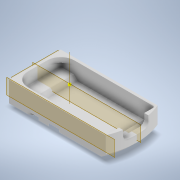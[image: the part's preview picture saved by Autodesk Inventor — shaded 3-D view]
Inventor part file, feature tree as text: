
AUTODESK INVENTOR PART (.ipt)
format: ipt  version: 2021 (Build 250183000, 183)  size: 813,056 bytes
history: native  units: in
note: dims shown in document units (in); Inventor stores cm internally (conversion verified against a paired STEP export)
features: sketch x10, extrude x9, fillet x4, chamfer x3, plane x3, mirror x2, other x1, pattern_circular x1
ambient origin geometry x8: Origin, YZ Plane, XZ Plane, XY Plane, X Axis, Y Axis, Z Axis, Center Point
bodies: Solid1 (feature_tree)
feature tree (33):
  extrude  "Extrusion1"  Depth=0.315in TaperAngle=0.0deg
  chamfer  "Chamfer2"  Distance=0.189in
  extrude  "Extrusion2"  Depth=0.1614in
  extrude  "Extrusion3"  Depth=0.2205in
  other  "Work Axis1"
  plane  "Work Plane1"
  extrude  "Extrusion5"  Depth=0.8268in
  extrude  "Extrusion4"  Depth=0.1969in
  fillet  "Fillet4"  Radius=0.063in
  pattern_circular  "Circular Pattern2"  [2 undecoded]
  fillet  "Fillet7"  [1 undecoded]
  extrude  "Extrusion9"  Depth=0.0394in
  extrude  "Extrusion10"  Depth=0.1181in TaperAngle=240.0deg
  fillet  "Fillet9"  Radius=0.0315in
  fillet  "Fillet10"  Radius=1.1811in
  mirror  "Mirror6"
  sketch  "Sketch18"  dims[d18=0.2047in d19=0.0in d23=0.8268in]
  chamfer  "Chamfer4"  Distance=0.5906in
  chamfer  "Chamfer5"  Distance=0.9728in
  plane  "Work Plane5"
  extrude  "Extrusion13"  Depth=0.4864in
  mirror  "Mirror7"
  plane  "Work Plane6"
  extrude  "Extrusion14"  Depth=0.0394in TaperAngle=0.0deg
  sketch  "Sketch1"  dims[d0=2.0472in d3=0.315in d4=0.0in]
  sketch  "Sketch2"  dims[d5=1.4315in]
  sketch  "Sketch3"  dims[d6=0.7079in]
  sketch  "Sketch4"  dims[d7=0.3539in]
  sketch  "Sketch7"  dims[d8=0.4882in d9=0.189in d10=0.0in]
  sketch  "Sketch12"  dims[d11=0.0in d14=0.1614in]
  sketch  "Sketch13"  dims[d15=0.0in d16=0.0in d17=0.2205in]
  sketch  "Sketch19"  dims[d24=0.3539in d31=0.1969in d32=0.063in d33=0.0in]
  sketch  "Sketch20"  dims[d44=0.1614in d47=0.0433in d48=0.0in d49=0.0in d51=0.0in d54=0.063in d55=0.0in d56=45.0deg d58=0.0394in d59=0.1181in d60=1.9685in d61=240.0deg d72=0.0315in d80=1.1811in d81=0.5906in d82=0.9728in d83=0.4864in d84=0.0394in d85=0.0in d86=0.547in d87=0.2735in d88=0.0787in d89=0.0in d90=0.0787in d98=0.1024in d99=0.0in d100=0.0in d101=0.2362in d102=0.0315in d103=0.0315in d104=0.2953in d105=0.1575in d106=0.1969in d107=0.063in d108=0.0787in d109=45.0deg d110=0.063in d111=0.0787in d112=45.0deg d114=0.3937in d115=0.0in d116=0.0in d117=-0.0394in d118=0.3937in d119=0.0in d91=0.0197in d92=0.0344in d93=0.0197in d94=0.0344in]
note: 3 required parameter values undecoded (feature->parameter linkage not recoverable at this tier; creation-order binding heuristic only, values carry confidence <= 0.55)
